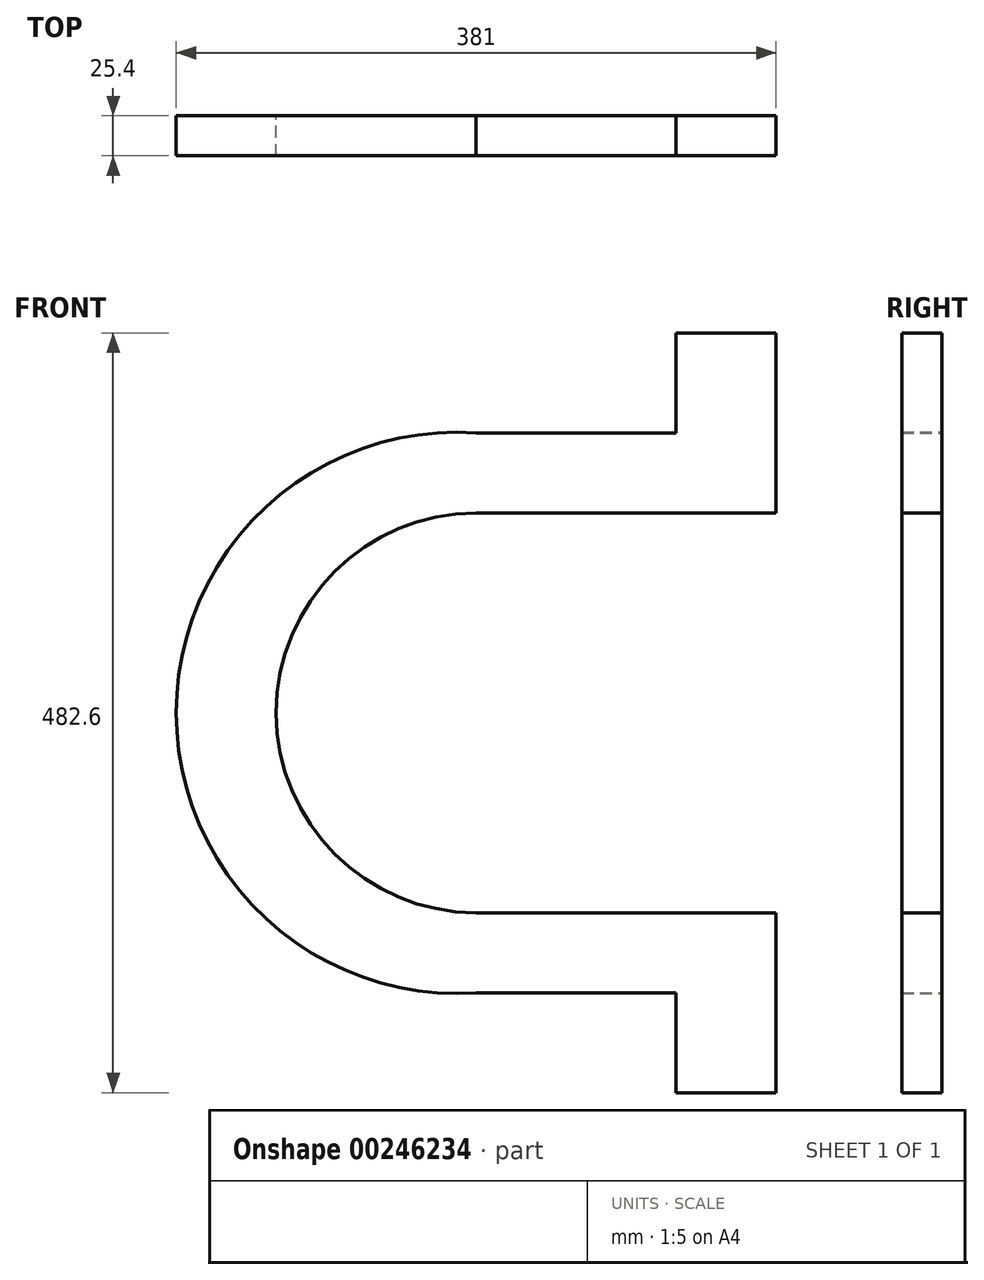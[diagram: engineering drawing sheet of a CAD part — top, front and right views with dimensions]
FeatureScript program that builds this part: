
annotation { "Feature Type Name" : "Feature", "Feature Type Description" : "" }
export const myFeature = defineFeature(function(context is Context, id is Id, definition is map)
    precondition{}
    {
        {
            var Q0;
            Q0=qCreatedBy(makeId("Front.planeOp"),FACE);
            var sketch = newSketch(context, id + "F0", { "sketchPlane" : qUnion([Q0])});
            skLineSegment(sketch, "E0.bottom", {"start": v(-24.55, 177.8) * mm, "end": v(127, 177.8) * mm});
            skLineSegment(sketch, "E0.top", {"start": v(-24.55, -177.8) * mm, "end": v(127, -177.8) * mm});
            skLineSegment(sketch, "E0.right", {"start": v(190.5, 177.8) * mm, "end": v(190.5, 127) * mm});
            skPoint(sketch, "E0.middle", {"position": v(0, 0) * mm});
            skArc(sketch, "E1", {"start": v(0, 127) * mm, "mid": v(-127, 0) * mm, "end": v(0, -127) * mm});
            skLineSegment(sketch, "E2", {"start": v(0, -127) * mm, "end": v(190.5, -127) * mm});
            skLineSegment(sketch, "E3.top", {"start": v(190.5, 241.3) * mm, "end": v(127, 241.3) * mm});
            skLineSegment(sketch, "E3.left", {"start": v(190.5, 177.8) * mm, "end": v(190.5, 241.3) * mm});
            skLineSegment(sketch, "E3.right", {"start": v(127, 177.8) * mm, "end": v(127, 241.3) * mm});
            skPoint(sketch, "E3.middle", {"position": v(158.75, 209.55) * mm});
            skLineSegment(sketch, "E4.top", {"start": v(190.5, -241.3) * mm, "end": v(127, -241.3) * mm});
            skLineSegment(sketch, "E4.left", {"start": v(190.5, -177.8) * mm, "end": v(190.5, -241.3) * mm});
            skLineSegment(sketch, "E4.right", {"start": v(127, -177.8) * mm, "end": v(127, -241.3) * mm});
            skPoint(sketch, "E4.middle", {"position": v(158.75, -209.55) * mm});
            skArc(sketch, "E5", {"start": v(0, 177.8) * mm, "mid": v(-190.5, 0) * mm, "end": v(0, -177.8) * mm});
            skPoint(sketch, "E5.first.point", {"position": v(0, -177.8) * mm});
            skPoint(sketch, "E5.second.point", {"position": v(-190.5, 0) * mm});
            skPoint(sketch, "E5.third.point", {"position": v(0, 177.8) * mm});
            skLineSegment(sketch, "E6", {"start": v(0, 127) * mm, "end": v(190.5, 127) * mm});
            skLineSegment(sketch, "E7.trimOffspring", {"start": v(190.5, -127) * mm, "end": v(190.5, -177.8) * mm});
            skPoint(sketch, "E8.orphan", {"position": v(-190.5, -177.8) * mm});
            skPoint(sketch, "E9.orphan", {"position": v(-190.5, 177.8) * mm});
            skLineSegment(sketch, "E10", {"start": v(0, -127) * mm, "end": v(0, -127) * mm});
            skSolve(sketch);
        }
        {
            var Q0;
            Q0 = qSketchRegion(id + "F0", true);
            extrude(context, id + "F1", {"entities" : qUnion([Q0]), "depth" : 25.4 * mm});
        }
    });
